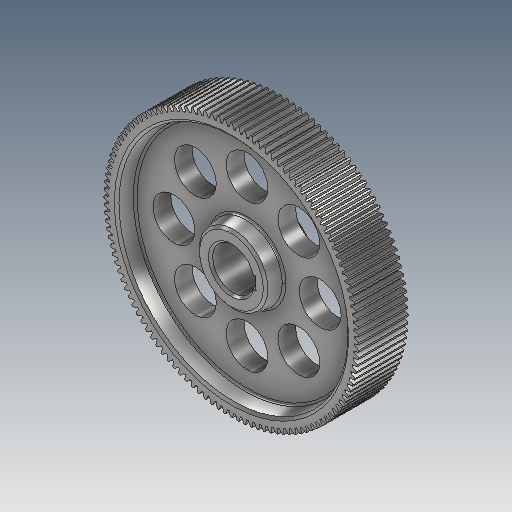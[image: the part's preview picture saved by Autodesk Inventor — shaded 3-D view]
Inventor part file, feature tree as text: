
AUTODESK INVENTOR PART (.ipt)
format: ipt  version: 2025 (Build 290162000, 162)  size: 855,040 bytes
history: native  units: mm (DEFAULTED — no unit token found)
features: other x5, sketch x5, extrude x4, plane x3, mirror x1, fillet x1, chamfer x1
ambient origin geometry x8: Origin, YZ Plane, XZ Plane, XY Plane, X Axis, Y Axis, Z Axis, Center Point
bodies: Solid1 (feature_tree)
feature tree (20):
  other  "{BB8FE430-83BF-418D-8DF9-9B323D3DB9B9}"
  extrude  "Extrusion1"  Depth=47.0mm TaperAngle=0.0deg
  plane  "Work Plane2"
  plane  "Work Plane8"
  plane  "Work Plane9"
  other  "正齿轮"
  extrude  "拉伸2"  Depth=10.0mm TaperAngle=0.0deg
  extrude  "拉伸3"  Depth=0.261799mm TaperAngle=0.0deg
  mirror  "镜像1"
  extrude  "拉伸4"  TaperAngle=0.0deg  [1 undecoded]
  other  "键槽2"
  fillet  "圆角1"  Radius=146.0mm
  chamfer  "倒角1"  [1 undecoded]
  sketch  "Sketch1"  dims[d0=244.0mm d1=47.0mm d2=0.0mm]
  other  "Srf1"
  sketch  "草图3"  dims[d16=146.0mm d17=0.0mm d34=0.261799mm]
  sketch  "草图4"  dims[d39=0.0mm d41=0.0mm d43=146.0mm]
  sketch  "草图5"  dims[d46=146.0mm d47=0.0mm d48=0.0mm d49=40.0mm d50=12.0mm d51=8.0mm d52=10.0mm d53=0.0mm d54=65.0mm d55=220.0mm d56=15.0mm d57=-2.007129mm d58=40.0mm d59=70.0mm d60=80.0mm d62=360.0deg d64=47.0mm d65=0.0mm d66=2.0mm d67=2.0mm d68=2.0mm d69=45.0deg]
  sketch  "草图 - 环形阵列1"  dims[d3=240.0mm d4=10.0mm d5=0.0mm]
  other  "轮毂键槽2"
note: 2 required parameter values undecoded (feature->parameter linkage not recoverable at this tier; creation-order binding heuristic only, values carry confidence <= 0.55)
